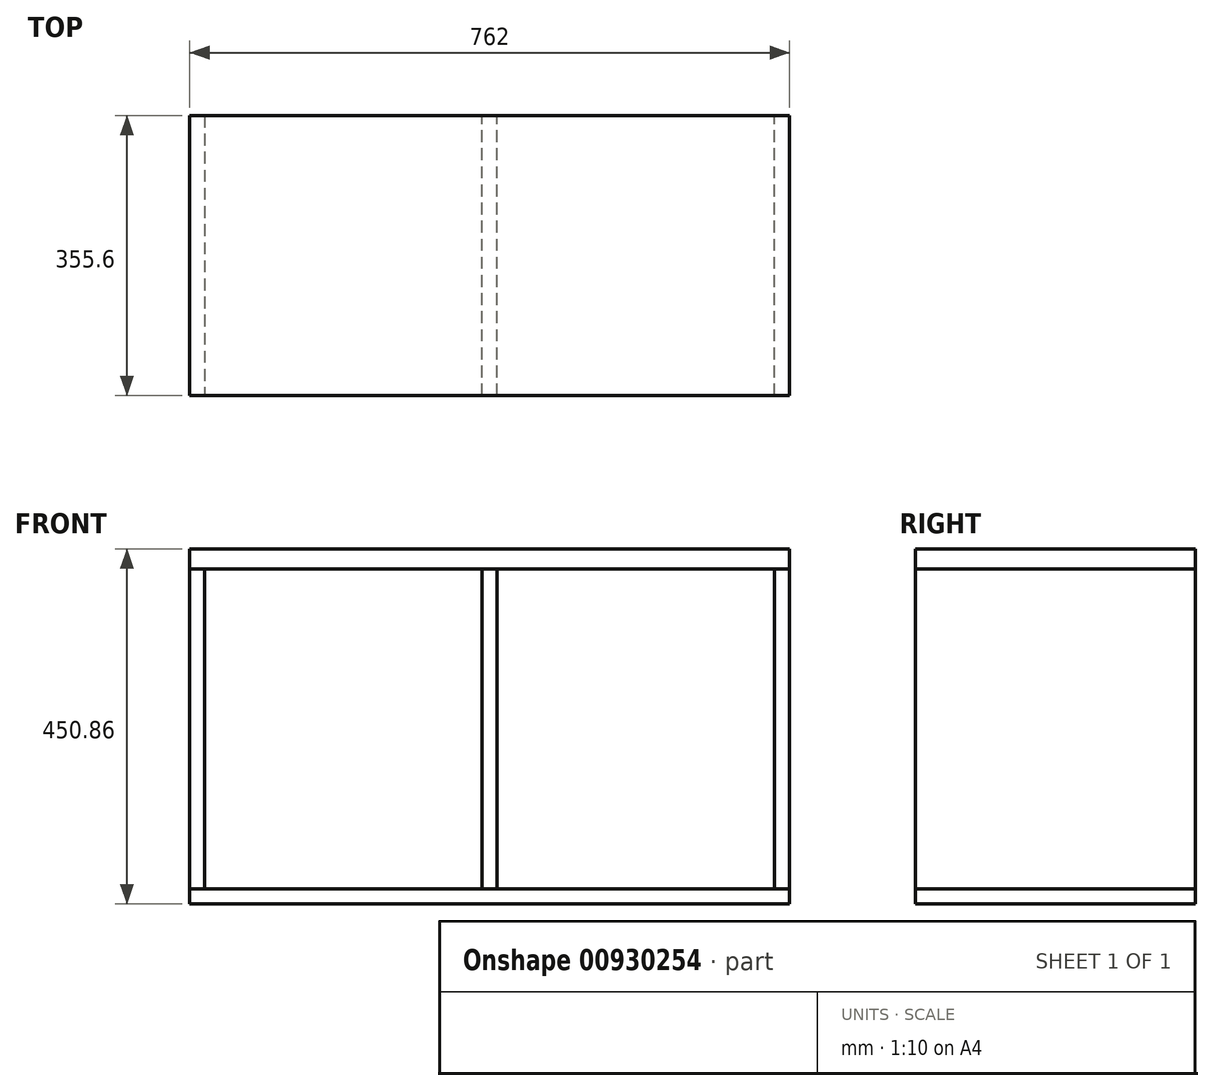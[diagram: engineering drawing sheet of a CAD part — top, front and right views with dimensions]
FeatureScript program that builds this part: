
annotation { "Feature Type Name" : "Feature", "Feature Type Description" : "" }
export const myFeature = defineFeature(function(context is Context, id is Id, definition is map)
    precondition{}
    {
        {
            var Q0;
            Q0=qCreatedBy(makeId("Top.planeOp"),FACE);
            var sketch = newSketch(context, id + "F0", { "sketchPlane" : qUnion([Q0])});
            skLineSegment(sketch, "E0.bottom", {"start": v(381, -177.8) * mm, "end": v(-381, -177.8) * mm});
            skLineSegment(sketch, "E0.top", {"start": v(381, 177.8) * mm, "end": v(-381, 177.8) * mm});
            skLineSegment(sketch, "E0.left", {"start": v(381, -177.8) * mm, "end": v(381, 177.8) * mm});
            skLineSegment(sketch, "E0.right", {"start": v(-381, -177.8) * mm, "end": v(-381, 177.8) * mm});
            skPoint(sketch, "E0.middle", {"position": v(0, 0) * mm});
            skSolve(sketch);
        }
        {
            var Q0;
            Q0=qSketchRegion(id+"F0",true);
            extrude(context, id + "F1", {"entities" : qUnion([Q0]), "endBound" : BoundingType.SYMMETRIC, "depth" : 19.05 * mm});
        }
        {
            var Q0;
            Q0=makeQuery(id+"F1.opExtrude","SWEPT_FACE",FACE,{"disambiguationData":[OSD([sQuery(id+"F0.wireOp",EDGE,"E0.left")])]});
            var sketch = newSketch(context, id + "F2", { "sketchPlane" : qUnion([Q0])});
            skLineSegment(sketch, "E1", {"start": v(177.8, 9.53) * mm, "end": v(177.8, 415.93) * mm});
            skLineSegment(sketch, "E2", {"start": v(-177.8, 415.93) * mm, "end": v(-177.8, 9.53) * mm});
            skLineSegment(sketch, "E3", {"start": v(-177.8, 9.53) * mm, "end": v(177.8, 9.53) * mm});
            skLineSegment(sketch, "E4", {"start": v(177.8, 415.93) * mm, "end": v(-177.8, 415.93) * mm});
            skSolve(sketch);
        }
        {
            var Q0;
            Q0=qSketchRegion(id+"F2",true);
            extrude(context, id + "F3", {"entities" : qUnion([Q0]), "oppositeDirection" : true, "depth" : 19.05 * mm});
        }
        {
            var Q0;
            Q0=qCreatedBy(makeId("Right.planeOp"),FACE);
            var sketch = newSketch(context, id + "F4", { "sketchPlane" : qUnion([Q0])});
            skLineSegment(sketch, "E5.0.0", {"start": v(-177.8, 9.53) * mm, "end": v(177.8, 9.53) * mm});
            skLineSegment(sketch, "E5.0.1", {"start": v(177.8, 9.53) * mm, "end": v(177.8, 415.93) * mm});
            skLineSegment(sketch, "E5.0.3", {"start": v(-177.8, 415.93) * mm, "end": v(-177.8, 9.53) * mm});
            skLineSegment(sketch, "E6", {"start": v(177.8, 415.93) * mm, "end": v(88.9, 415.93) * mm});
            skLineSegment(sketch, "E7", {"start": v(88.9, 415.93) * mm, "end": v(-177.8, 415.93) * mm});
            skSolve(sketch);
        }
        {
            var Q0;
            Q0=qSketchRegion(id+"F4",true);
            extrude(context, id + "F5", {"entities" : qUnion([Q0]), "endBound" : BoundingType.SYMMETRIC, "depth" : 19.05 * mm});
        }
        {
            var Q0;
            Q0=makeQuery(id+"F1.opExtrude","SWEPT_FACE",FACE,{"disambiguationData":[OSD([sQuery(id+"F0.wireOp",EDGE,"E0.right")])]});
            var sketch = newSketch(context, id + "F6", { "sketchPlane" : qUnion([Q0])});
            skLineSegment(sketch, "E8.0.0", {"start": v(177.8, 415.93) * mm, "end": v(177.8, 9.53) * mm});
            skLineSegment(sketch, "E8.0.1", {"start": v(177.8, 9.53) * mm, "end": v(-177.8, 9.53) * mm});
            skLineSegment(sketch, "E8.0.2", {"start": v(-177.8, 9.53) * mm, "end": v(-177.8, 415.93) * mm});
            skLineSegment(sketch, "E8.0.3", {"start": v(-177.8, 415.93) * mm, "end": v(177.8, 415.93) * mm});
            skSolve(sketch);
        }
        {
            var Q0;
            Q0=qSketchRegion(id+"F6",true);
            extrude(context, id + "F7", {"entities" : qUnion([Q0]), "oppositeDirection" : true, "depth" : 19.05 * mm});
        }
        {
            var Q0;
            Q0=makeQuery(id+"F7.opExtrude","SWEPT_FACE",FACE,{"disambiguationData":[OSD([sQuery(id+"F6.wireOp",EDGE,"E8.0.3")])]});
            var sketch = newSketch(context, id + "F8", { "sketchPlane" : qUnion([Q0])});
            skLineSegment(sketch, "E9.0.0", {"start": v(-381, -177.8) * mm, "end": v(381, -177.8) * mm});
            skLineSegment(sketch, "E9.0.1", {"start": v(381, -177.8) * mm, "end": v(381, 177.8) * mm});
            skLineSegment(sketch, "E9.0.2", {"start": v(381, 177.8) * mm, "end": v(-381, 177.8) * mm});
            skLineSegment(sketch, "E9.0.3", {"start": v(-381, 177.8) * mm, "end": v(-381, -177.8) * mm});
            skSolve(sketch);
        }
        {
            var Q0;
            Q0=qSketchRegion(id+"F8",true);
            extrude(context, id + "F9", {"entities" : qUnion([Q0]), "depth" : 25.4 * mm});
        }
    });
